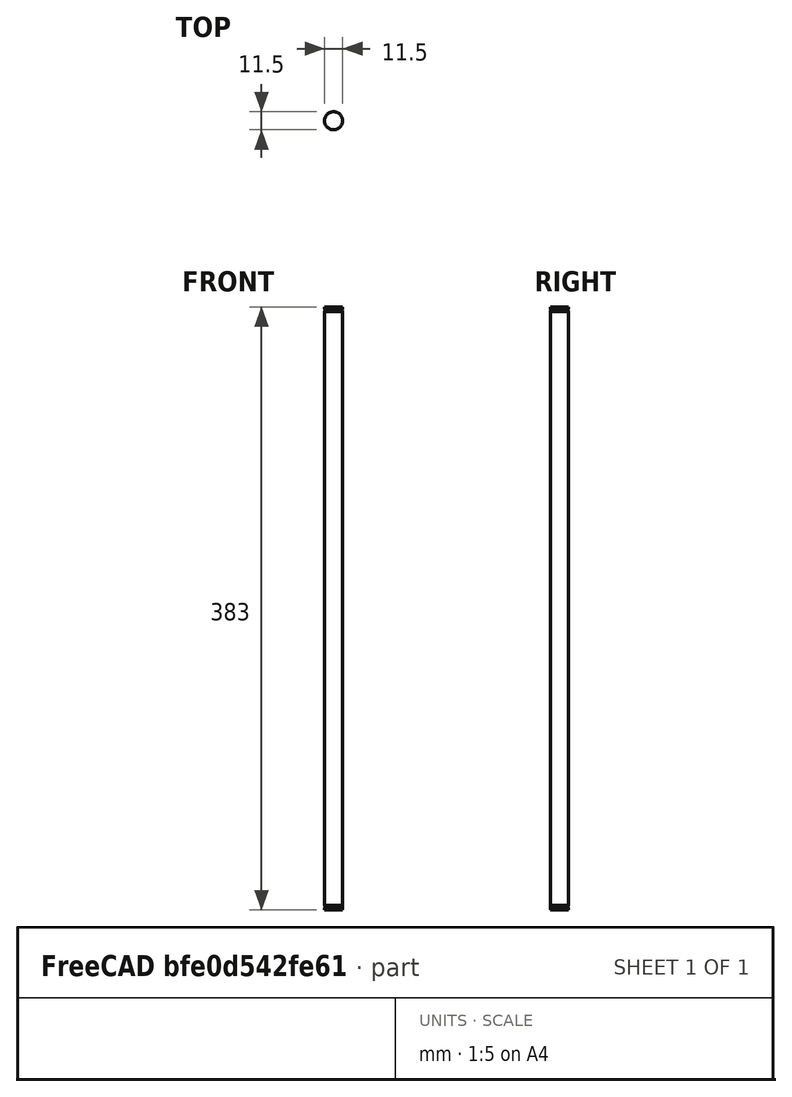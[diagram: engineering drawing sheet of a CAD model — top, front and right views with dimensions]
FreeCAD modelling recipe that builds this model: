
FCSTD DOCUMENT  (FreeCAD 0.18R16110 (Git))
Label: cylinder1
License: All rights reserved
LicenseURL: http://en.wikipedia.org/wiki/All_rights_reserved
objects: Part::Torus×2, Part::Cut×2, Part::Cylinder×1
note: 5 computed .brp shape members not serialized (recipe doc carries the construction recipe); baked Part::Feature solids carry a one-line shape summary decoded from their .brp

FEATURE [Part::Cylinder] Cylinder
  Angle = 360
  AttacherType = Attacher::AttachEngine3D
  Height = 383
  Radius = 5.75
FEATURE [Part::Torus] Torus
  Angle1 = -180
  Angle2 = 180
  Angle3 = 360
  AttacherType = Attacher::AttachEngine3D
  Placement = pos=(0,0,2) rot=(0,0,1;0rad)
  Radius1 = 7.5
  Radius2 = 2
FEATURE [Part::Cut] Cut
  Base = -> Cylinder
  Tool = -> Torus
FEATURE [Part::Torus] Torus001
  Angle1 = -180
  Angle2 = 180
  Angle3 = 360
  AttacherType = Attacher::AttachEngine3D
  Placement = pos=(0,0,381) rot=(0,0,1;0rad)
  Radius1 = 7.5
  Radius2 = 2
FEATURE [Part::Cut] Cut001
  Base = -> Cut
  Tool = -> Torus001
